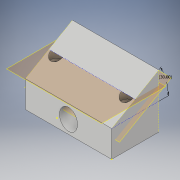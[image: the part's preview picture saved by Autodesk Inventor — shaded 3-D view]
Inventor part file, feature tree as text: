
AUTODESK INVENTOR PART (.ipt)
format: ipt  version: 2019.4 (Build 234330000, 330)  size: 148,992 bytes
history: native  units: in
note: dims shown in document units (in); Inventor stores cm internally (conversion verified against a paired STEP export)
features: sketch x6, plane x2, other x2, loft x1, extrude x1, hole x1, split x1
ambient origin geometry x8: Origin, YZ Plane, XZ Plane, XY Plane, X Axis, Y Axis, Z Axis, Center Point
bodies: Solid1 (feature_tree)
feature tree (14):
  sketch  "Sketch2"  dims[d2=2.75in d4=-3.0in]
  plane  "Work Plane1"
  loft  "Loft1"
  sketch  "Sketch4"  dims[d9=0.0in d10=90.0deg d11=30.0deg]
  sketch  "Sketch5"  dims[d12=90.0deg]
  plane  "Work Plane2"
  extrude  "Extrusion1"  TaperAngle=0.0deg  [1 undecoded]
  other  "centerLineForHoleWork Plane"
  other  "screwHoleWork Plane"
  hole  "Hole1"  [1 undecoded]
  split  "Split1"
  sketch  "Sketch3"  dims[d5=2.75in d7=0.0in d8=90.0deg]
  sketch  "Sketch6"  dims[d15=1.0in d16=0.0in]
  sketch  "Sketch7"  dims[d17=-0.75in d18=2.25in d19=2.25in d20=0.281in d21=0.75in d22=0.75in d23=0.5in d24=90.0deg d25=1.0in d26=0.8108in]
note: 2 required parameter values undecoded (feature->parameter linkage not recoverable at this tier; creation-order binding heuristic only, values carry confidence <= 0.55)
